# Revit family: Basin-Wall_Mounted-American_Standard-Corner_Minette-0451_Series
name_source: partatom
category: Plumbing Fixtures
revit_build: Autodesk Revit 2014 (Build: 20130308_1515(x64)
units: mm (PartAtom-declared; Revit-internal decimal feet)

## types (8) — shared parameters
Assembly Code = D2010310
Basin Shape = D-Shaped
CW Connection = Yes
CWFU = 1.5
Cold Water Connection Diameter = 3/8"
Cold Water Connection Height = 20 3/4"
Cold Water Connection Radius = 3/16"
Cold Water Connection Width = 4"
Default Elevation = 31"
HW Connection = Yes
HWFU = 1.5
Height = 7"
Hot Water Connection Diameter = 3/8"
Hot Water Connection Height = 20 3/4"
Hot Water Connection Radius = 3/16"
Hot Water Connection Width = 4"
Installation Type = Wall Hung
Length = 11"
Manufacturer = American Standard
Price = Prices may vary. Please consult Manufacturer Representative for most up-to-date price list.
Product Documentation Link = https://www.americanstandard-us.com
Product Page URL = https://www.americanstandard-us.com
Revised Date = 12/12/2018
Shipping Weight = 17lbs (8kg)
URL = http://www.americanstandard-us.com
Vent Connection = No
WFU = 2
Warranty Information = 1 Year Limited
Waste Connection = Yes
Waste Connection Diameter = 1 1/4"
Waste Connection Height = 18 1/4"
Waste Connection Radius = 5/8"
Width = 11"

## per-type parameters (varying)
| type | Description | Faucet Holes | Finish | Hole Punch Location | Material |
| 0451.021.020 | Corner Minette Wall Mounted Sink with faucet holes on 4" (102mm) centers. | Yes | Vitreous China-American Standard-020-White | 4" | Vitreous China-American Standard-020-White |
| 0451.001.020 | Corner Minette Wall Mounted Sink with single center faucet hole. | No | Vitreous China-American Standard-020-White | 20" | Vitreous China-American Standard-020-White |
| 0451.001.021 | Corner Minette Wall Mounted Sink with single center faucet hole. | No | Vitreous China-American Standard-021-Bone | 20" | Vitreous China-American Standard-021-Bone |
| 0451.001.178 | Corner Minette Wall Mounted Sink with single center faucet hole. | No | Vitreous China-American Standard-178-Black | 20" | Vitreous China-American Standard-178-Black |
| 0451.001.222 | Corner Minette Wall Mounted Sink with single center faucet hole. | No | Vitreous China-American Standard-222-Linen | 20" | Vitreous China-American Standard-222-Linen |
| 0451.021.021 | Corner Minette Wall Mounted Sink with faucet holes on 4" (102mm) centers. | Yes | Vitreous China-American Standard-021-Bone | 4" | Vitreous China-American Standard-021-Bone |
| 0451.021.178 | Corner Minette Wall Mounted Sink with faucet holes on 4" (102mm) centers. | Yes | Vitreous China-American Standard-178-Black | 4" | Vitreous China-American Standard-178-Black |
| 0451.021.222 | Corner Minette Wall Mounted Sink with faucet holes on 4" (102mm) centers. | Yes | Vitreous China-American Standard-222-Linen | 4" | Vitreous China-American Standard-222-Linen |

note: column(s) folded — value = type name in every type: Model

## geometry (parser evidence)
native form markers: Sweep x3
no freeform markers — native parametric forms only
